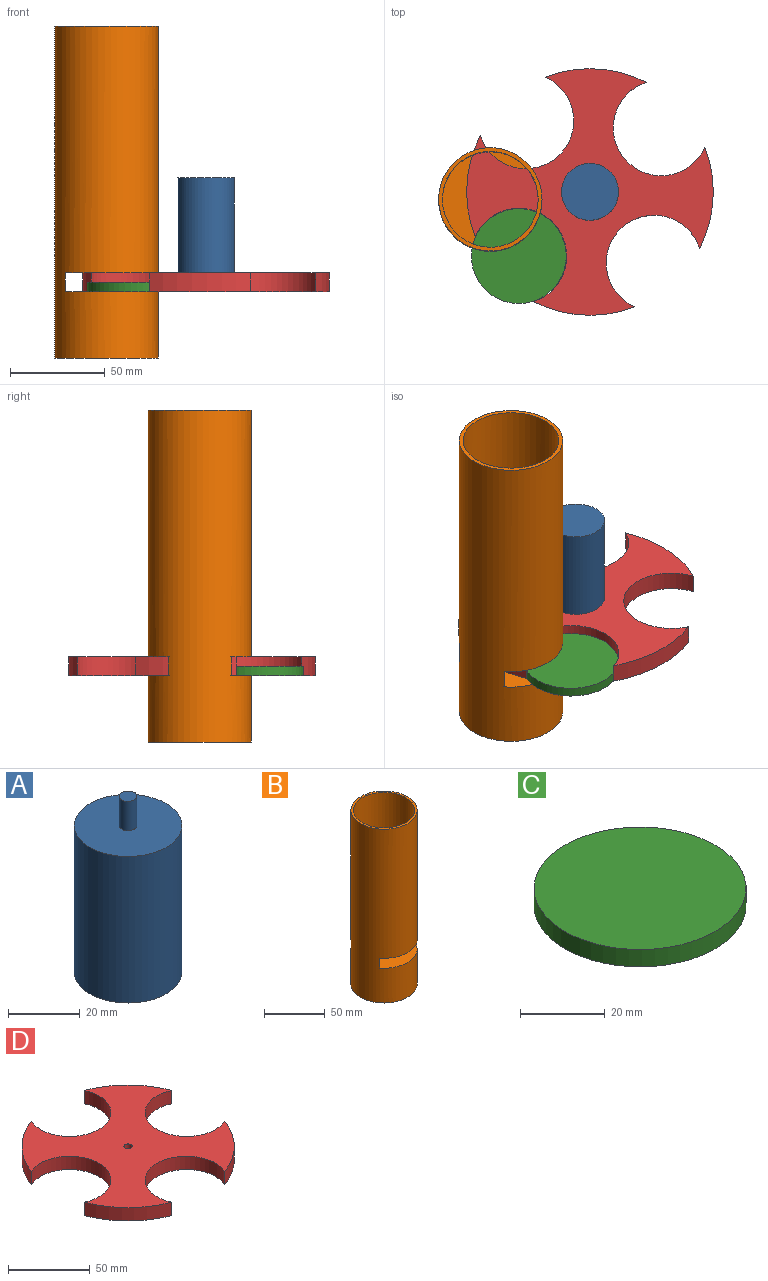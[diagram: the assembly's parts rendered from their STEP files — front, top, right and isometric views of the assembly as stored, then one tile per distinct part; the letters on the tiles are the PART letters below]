
ASSEMBLY  parts=4 mates=5
PART A: 5 faces, bbox 30x30x60 mm
  f0: cylinder r=15mm len=50mm, axis (0,0,-1), area 4712.4mm2, adj f1,f2
  f1: plane 30x30mm, normal (0,0,1), area 687.2mm2, adj f0,f3
  f2: plane 30x30mm, normal (0,0,-1), area 706.9mm2, adj f0
  f3: cylinder r=2.5mm len=10mm, axis (0,0,-1), area 157.1mm2, adj f1,f4
  f4: plane 5x5mm, normal (0,0,1), area 19.6mm2, adj f3
PART B: 8 faces, bbox 54.5x54.5x175 mm
  f0: cylinder r=25.25mm len=140mm, axis (0,0,-1), area 20898mm2, adj f2,f3,f4,f5,f6
  f1: cylinder r=27.25mm len=175mm, axis (0,0,-1), area 28606.9mm2, adj f2,f3,f4,f5,f6,f7
  f2: plane 54.5x54.5mm, normal (0,0,1), area 329.9mm2, adj f0,f1
  f3: plane 10x3.55mm, normal (1,0,0), area 35.5mm2, adj f0,f1,f5,f6
  f4: plane 10x3.55mm, normal (1,0,0), area 35.5mm2, adj f0,f1,f5,f6
  f5: plane 54.5x48.89mm, normal (0,0,-1), area 266.8mm2, adj f0,f1,f3,f4
  f6: plane 54.5x52.5mm, normal (0,0,1), area 2269.7mm2, adj f0,f1,f3,f4
  f7: plane 54.5x54.5mm, normal (0,0,-1), area 2332.8mm2, adj f1
PART C: 3 faces, bbox 50x50x5 mm
  f0: cylinder r=25mm len=50mm, axis (0,0,-1), area 785.4mm2, adj f1,f2
  f1: plane 50x50mm, normal (0,0,1), area 1963.5mm2, adj f0
  f2: plane 50x50mm, normal (0,0,-1), area 1963.5mm2, adj f0
PART D: 11 faces, bbox 121.5x121.5x10 mm
  f0: cylinder r=25.25mm len=50.5mm, axis (0,0,-1), area 1004.8mm2, adj f1,f7,f9,f10
  f1: cylinder r=65mm len=37.7mm, axis (0,0,-1), area 549.4mm2, adj f0,f2,f9,f10
  f2: cylinder r=25.25mm len=50.5mm, axis (0,0,-1), area 1004.8mm2, adj f1,f3,f9,f10
  f3: cylinder r=65mm len=37.7mm, axis (0,0,-1), area 549.4mm2, adj f2,f4,f9,f10
  f4: cylinder r=25.25mm len=50.5mm, axis (0,0,-1), area 1004.8mm2, adj f3,f5,f9,f10
  f5: cylinder r=65mm len=37.7mm, axis (0,0,-1), area 549.4mm2, adj f4,f6,f9,f10
  f6: cylinder r=25.25mm len=50.5mm, axis (0,0,-1), area 1004.8mm2, adj f5,f7,f9,f10
  f7: cylinder r=65mm len=37.7mm, axis (0,0,-1), area 549.4mm2, adj f0,f6,f9,f10
  f8: cylinder r=2.5mm len=10mm, axis (0,0,-1), area 157.1mm2, adj f9,f10
  f9: plane 121.54x121.54mm, normal (0,0,1), area 6708mm2, adj f0,f1,f2,f3,f4,f5,f6,f7
  f10: plane 121.54x121.54mm, normal (0,0,-1), area 6708mm2, adj f0,f1,f2,f3,f4,f5,f6,f7
PLACE A rot(axis=(1,0,0),180deg) t=(52.54,4.11,70)mm fixed
PLACE B at identity fixed
PLACE C rot(axis=(0,0,1),39.4deg) t=(15.01,-29.69,10)mm
PLACE D rot(axis=(0,0,1),132deg) t=(52.54,4.11,10)mm
MATE planar D.f1 <-> B.f0  axis (0,0,1) through (52.54,4.11,20)mm
MATE cylindrical A.f3 <-> D.f1  axis (0,0,1) through (52.54,4.11,15)mm
MATE cylindrical C.f0 <-> D.f2  axis (0,0,1) through (15.01,-29.69,15)mm
MATE planar A.f0 <-> B.f5  axis (0,0,-1) through (52.54,4.11,20)mm
MATE planar C.f0 <-> D.f10  axis (0,0,-1) through (15.01,-29.69,10)mm
